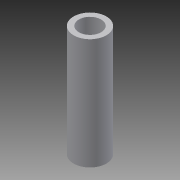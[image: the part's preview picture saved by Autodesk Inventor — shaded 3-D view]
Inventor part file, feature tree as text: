
AUTODESK INVENTOR PART (.ipt)
format: ipt  version: 2013 (Build 170138000, 138)  size: 67,584 bytes
history: native  units: mm
features: extrude x1, sketch x1
ambient origin geometry x8: Origin, YZ Plane, XZ Plane, XY Plane, X Axis, Y Axis, Z Axis, Center Point
bodies: Volumenkörper1 (feature_tree)
feature tree (2):
  extrude  "Extrusion1"  Depth=5.9mm
  sketch  "Skizze1"  dims[d0=4.0mm d1=5.9mm d2=20.0mm d3=0.0mm]
